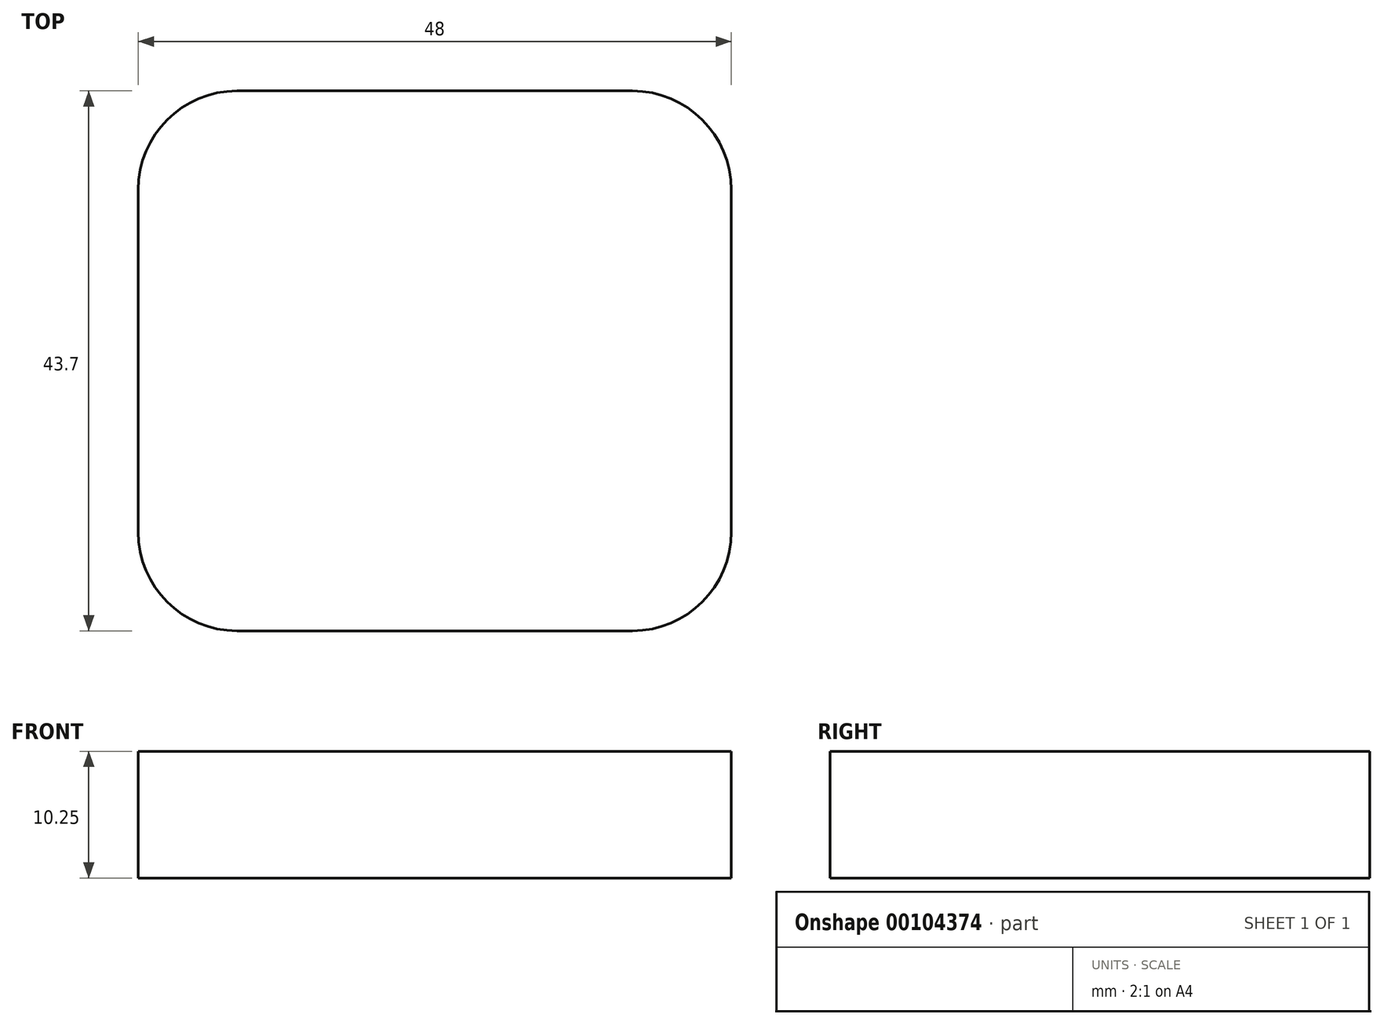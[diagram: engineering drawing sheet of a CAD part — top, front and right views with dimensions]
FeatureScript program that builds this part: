
annotation { "Feature Type Name" : "Feature", "Feature Type Description" : "" }
export const myFeature = defineFeature(function(context is Context, id is Id, definition is map)
    precondition{}
    {
        {
            var Q0;
            Q0=qCreatedBy(makeId("Top.planeOp"),FACE);
            var sketch = newSketch(context, id + "F0", { "sketchPlane" : qUnion([Q0])});
            skLineSegment(sketch, "E0.bottom", {"start": v(-16, 21.75) * mm, "end": v(16, 21.75) * mm});
            skLineSegment(sketch, "E0.top", {"start": v(-16, -21.95) * mm, "end": v(16, -21.95) * mm});
            skLineSegment(sketch, "E0.left", {"start": v(-24, 13.75) * mm, "end": v(-24, -13.95) * mm});
            skLineSegment(sketch, "E0.right", {"start": v(24, 13.75) * mm, "end": v(24, -13.95) * mm});
            skPoint(sketch, "E1.visualSharp", {"position": v(24, 21.75) * mm});
            skArc(sketch, "E1.filletArc", {"start": v(24, 13.75) * mm, "mid": v(21.66, 19.4) * mm, "end": v(16, 21.75) * mm});
            skPoint(sketch, "E2.visualSharp", {"position": v(24, -21.95) * mm});
            skArc(sketch, "E2.filletArc", {"start": v(16, -21.95) * mm, "mid": v(21.66, -19.6) * mm, "end": v(24, -13.95) * mm});
            skPoint(sketch, "E3.visualSharp", {"position": v(-24, -21.95) * mm});
            skArc(sketch, "E3.filletArc", {"start": v(-24, -13.95) * mm, "mid": v(-21.66, -19.6) * mm, "end": v(-16, -21.95) * mm});
            skPoint(sketch, "E4.visualSharp", {"position": v(-24, 21.75) * mm});
            skArc(sketch, "E4.filletArc", {"start": v(-16, 21.75) * mm, "mid": v(-21.66, 19.4) * mm, "end": v(-24, 13.75) * mm});
            skSolve(sketch);
        }
        {
            var Q0;
            Q0=makeQuery(id+"F0.imprint","IMPRINT",FACE,{"disambiguationData":[TD([[makeQuery(id+"F0.imprint","IMPRINT",EDGE,{"derivedFrom":sQuery(id+"F0.wireOp",EDGE,"E0.bottom")}),-1.0]])]});
            extrude(context, id + "F1", {"entities" : qUnion([Q0]), "depth" : 10.25 * mm});
        }
    });
